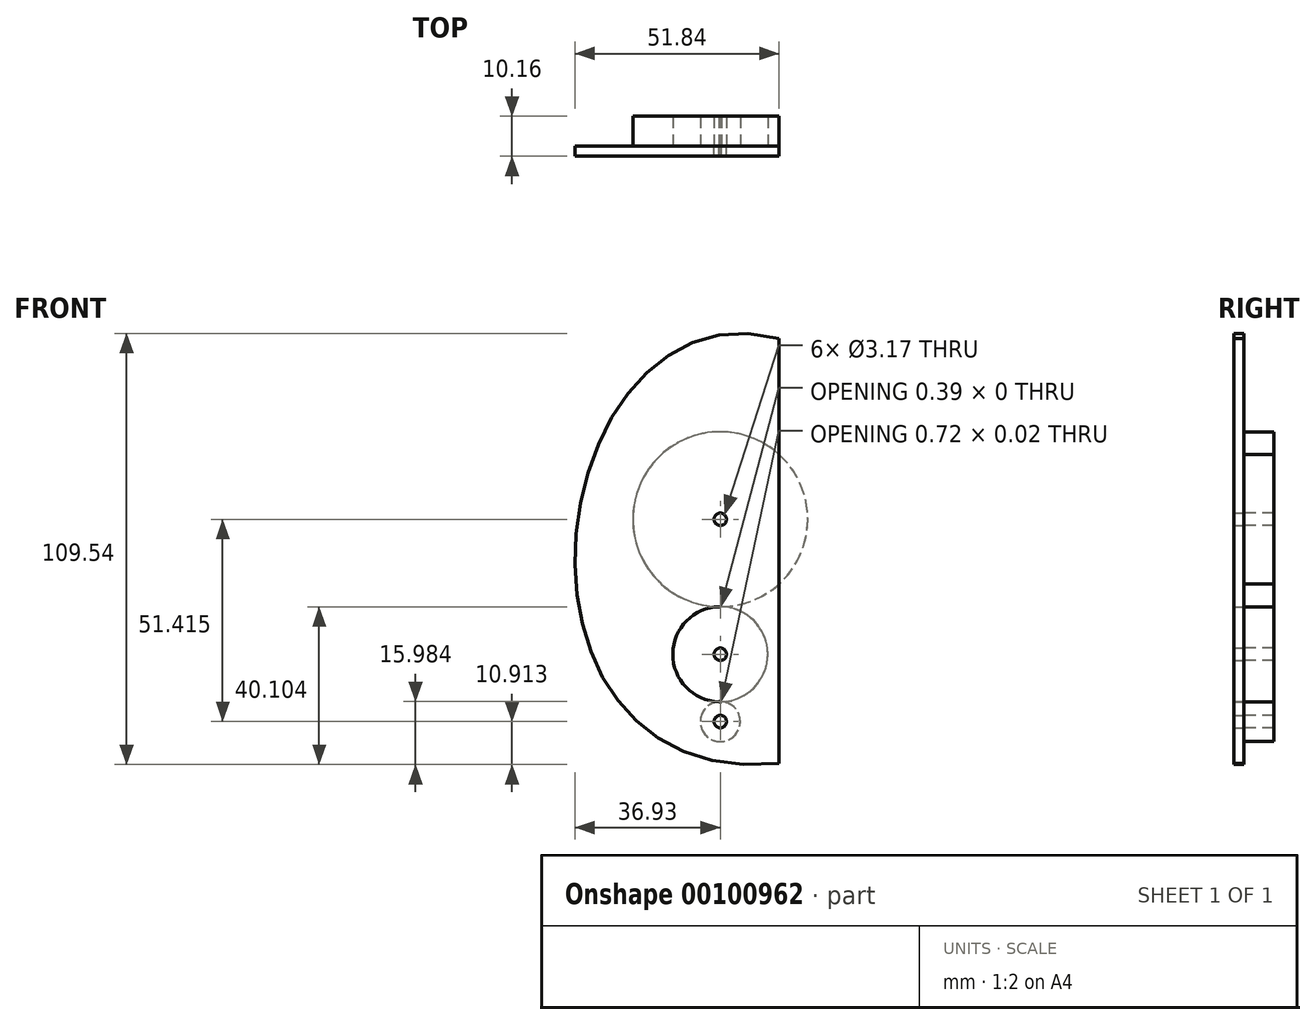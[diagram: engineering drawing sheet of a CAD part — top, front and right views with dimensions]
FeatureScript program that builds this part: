
annotation { "Feature Type Name" : "Feature", "Feature Type Description" : "" }
export const myFeature = defineFeature(function(context is Context, id is Id, definition is map)
    precondition{}
    {
        {
            var Q0;
            Q0=qCreatedBy(makeId("Front.planeOp"),FACE);
            var sketch = newSketch(context, id + "F0", { "sketchPlane" : qUnion([Q0])});
            skLineSegment(sketch, "E0.right", {"start": v(14.91, 94.42) * mm, "end": v(14.91, -13.53) * mm});
            skCircle(sketch, "E1", {"center": v(0, 48.47) * mm, "radius": 22.23 * mm});
            skCircle(sketch, "E2", {"center": v(0, 14.18) * mm, "radius": 12.07 * mm});
            skCircle(sketch, "E3", {"center": v(0, 48.47) * mm, "radius": 1.59 * mm});
            skCircle(sketch, "E4", {"center": v(0, 14.18) * mm, "radius": 1.59 * mm});
            skCircle(sketch, "E5", {"center": v(0, -2.95) * mm, "radius": 5.08 * mm});
            skCircle(sketch, "E6", {"center": v(0, -2.95) * mm, "radius": 1.59 * mm});
            skPoint(sketch, "E7", {"position": v(-36.87, 41.15) * mm});
            skFitSpline(sketch, "E8", {"points": [v(14.91, 94.42) * mm, v(-36.87, 41.15) * mm, v(14.91, -13.53) * mm], "startDerivative": vector(-188.31, 48.06) * mm, "endDerivative": vector(215.95, 22.53) * mm});
            skSolve(sketch);
        }
        {
            var Q0;
            Q0=makeQuery(id+"F0.imprint","IMPRINT",FACE,{"disambiguationData":[TD([[makeQuery(id+"F0.imprint","IMPRINT",EDGE,{"derivedFrom":sQuery(id+"F0.wireOp",EDGE,"E0.bottom")}),-1.0]])]});
            var Q1;
            {var subQ5=sQuery(id+"F0.wireOp",EDGE,"E8");Q1=makeQuery(id+"F0.imprint","IMPRINT",FACE,{"disambiguationData":[TD([[makeQuery(id+"F0.imprint","IMPRINT",EDGE,{"derivedFrom":subQ5}),1.0]])]});}
            var Q2;
            Q2=makeQuery(id+"F0.imprint","IMPRINT",FACE,{"disambiguationData":[TD([[makeQuery(id+"F0.imprint","IMPRINT",EDGE,{"derivedFrom":sQuery(id+"F0.wireOp",EDGE,"E3")}),-1.0]])]});
            var Q3;
            Q3=makeQuery(id+"F0.imprint","IMPRINT",FACE,{"disambiguationData":[TD([[makeQuery(id+"F0.imprint","IMPRINT",EDGE,{"derivedFrom":sQuery(id+"F0.wireOp",EDGE,"E4")}),-1.0]])]});
            var Q4;
            Q4=makeQuery(id+"F0.imprint","IMPRINT",FACE,{"disambiguationData":[TD([[makeQuery(id+"F0.imprint","IMPRINT",EDGE,{"derivedFrom":sQuery(id+"F0.wireOp",EDGE,"E6")}),-1.0]])]});
            extrude(context, id + "F1", {"entities" : qUnion([Q0, Q1, Q2, Q3, Q4]), "depth" : 2.54 * mm});
        }
        {
            var Q0;
            Q0=makeQuery(id+"F0.imprint","IMPRINT",FACE,{"disambiguationData":[TD([[makeQuery(id+"F0.imprint","IMPRINT",EDGE,{"derivedFrom":sQuery(id+"F0.wireOp",EDGE,"E3")}),-1.0]])]});
            var Q1;
            {var subQ0=sQuery(id+"F0.wireOp",EDGE,"E1");var subQ1=sQuery(id+"F0.wireOp",EDGE,"E0.right");var subQ2=makeQuery(id+"F0.imprint","INTERSECT",VERTEX,{"disambiguationData":[OD(0.0)],"derivedFrom":[subQ1,subQ0]});Q1=makeQuery(id+"F0.imprint","IMPRINT",FACE,{"disambiguationData":[TD([[makeQuery(id+"F0.imprint","IMPRINT",EDGE,{"disambiguationData":[TD([[subQ2,-1.0]])],"derivedFrom":subQ1}),1.0]])]});}
            extrude(context, id + "F2", {"entities" : qUnion([Q0, Q1]), "oppositeDirection" : true, "depth" : 7.62 * mm});
        }
        {
            var Q0;
            Q0=makeQuery(id+"F0.imprint","IMPRINT",FACE,{"disambiguationData":[TD([[makeQuery(id+"F0.imprint","IMPRINT",EDGE,{"derivedFrom":sQuery(id+"F0.wireOp",EDGE,"E4")}),-1.0]])]});
            extrude(context, id + "F3", {"entities" : qUnion([Q0]), "oppositeDirection" : true, "depth" : 7.62 * mm});
        }
        {
            var Q0;
            Q0=makeQuery(id+"F0.imprint","IMPRINT",FACE,{"disambiguationData":[TD([[makeQuery(id+"F0.imprint","IMPRINT",EDGE,{"derivedFrom":sQuery(id+"F0.wireOp",EDGE,"E6")}),-1.0]])]});
            extrude(context, id + "F4", {"entities" : qUnion([Q0]), "oppositeDirection" : true, "depth" : 7.62 * mm});
        }
    });
